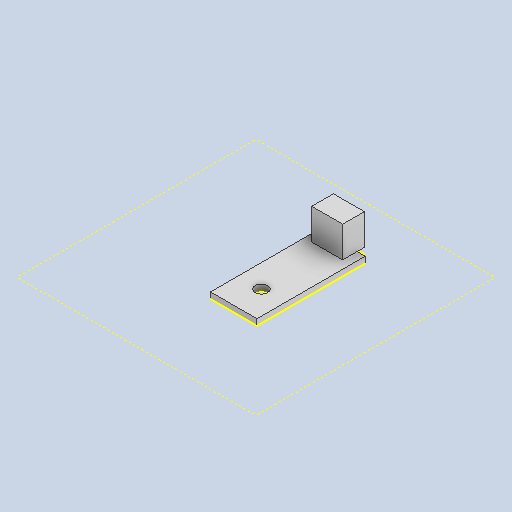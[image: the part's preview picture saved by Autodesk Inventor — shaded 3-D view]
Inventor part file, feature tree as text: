
AUTODESK INVENTOR PART (.ipt)
format: ipt  version: 2025.1 (Build 291241000, 241)  size: 94,208 bytes
history: native  units: in
note: dims shown in document units (in); Inventor stores cm internally (conversion verified against a paired STEP export)
features: other x3, sketch x1
ambient origin geometry x8: Origin, YZ Plane, XZ Plane, XY Plane, X Axis, Y Axis, Z Axis, Center Point
bodies: Solid1 (feature_tree)
feature tree (4):
  other  "Sensor ky-037_MIR.ipt"
  other  "Solid1::Sensor ky-037_MIR.ipt"
  other  "TaggingFeature1"
  sketch  "Sketch1"  dims[d0=0.3937in]
